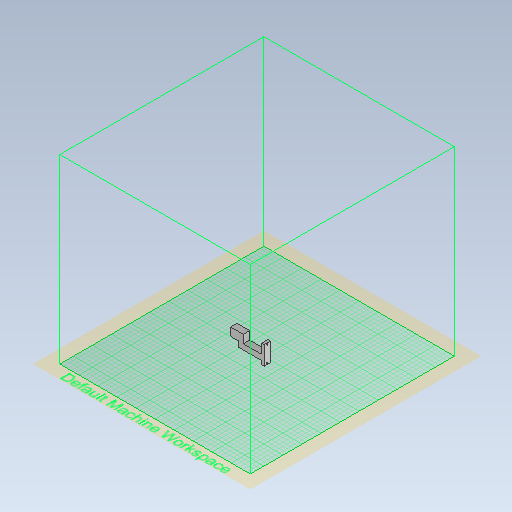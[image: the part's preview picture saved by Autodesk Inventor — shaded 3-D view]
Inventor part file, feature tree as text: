
AUTODESK INVENTOR PART (.ipt)
format: ipt  version: 2020.3 (Build 243373000, 373)  size: 288,768 bytes
history: native  units: mm
features: extrude x3, sketch x2, fillet x1
ambient origin geometry x8: Origin, YZ Plane, XZ Plane, XY Plane, X Axis, Y Axis, Z Axis, Center Point
bodies: Body1 (feature_tree)
feature tree (6):
  sketch  "Sketch1"  dims[d12=14.0mm d13=30.0mm]
  extrude  "Extrusion6"  Depth=30.0mm
  extrude  "Extrusion7"  TaperAngle=0.0deg  [1 undecoded]
  fillet  "Fillet2"  Radius=10.0mm
  extrude  "Extrusion9"  Depth=10.0mm TaperAngle=0.0deg
  sketch  "Sketch7"  dims[d14=12.0mm d15=0.0mm d16=10.0mm d17=0.0mm d18=10.0mm d19=0.0mm d29=18.0mm d30=0.0mm d31=5.0mm d32=41.0mm d33=5.0mm d34=14.0mm d35=2.8mm d36=3.0mm d37=2.8mm d38=35.0mm d39=6.0mm d40=0.0mm]
note: 1 required parameter value undecoded (feature->parameter linkage not recoverable at this tier; creation-order binding heuristic only, values carry confidence <= 0.55)
